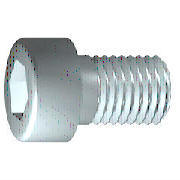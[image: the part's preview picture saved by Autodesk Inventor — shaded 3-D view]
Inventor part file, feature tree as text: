
AUTODESK INVENTOR PART (.ipt)
format: ipt  version: 2019 (Build 230136000, 136)  size: 200,192 bytes
history: native  units: mm (DEFAULTED — no unit token found)
features: sketch x2, extrude x1, plane x1, fillet x1
ambient origin geometry x7: Origin, YZ Plane, XY Plane, X Axis, Y Axis, Z Axis, Center Point
bodies: Solid1 (feature_tree), Body (feature_tree)
feature tree (5):
  extrude  "Slot"  Depth=1.6mm
  plane  "Work Plane1"
  fillet  "Fillet2"  Radius=1.6mm
  sketch  "Sketch1"  dims[d1=1.45mm d2=0.214807mm d3=1.6mm]
  sketch  "Sketch2"  dims[d4=0.7mm d5=60.0deg d6=1.6mm d7=1.6mm d8=1.732051mm d9=3.0mm d10=90.0deg d11=10.0mm d12=0.0mm d13=1.45mm d14=0.0mm d15=0.214707mm d16=0.214707mm d17=0.16mm d19=0.0mm d26=2.5mm d27=45.0deg d28=0.0mm d29=0.0mm d30=0.1mm]
